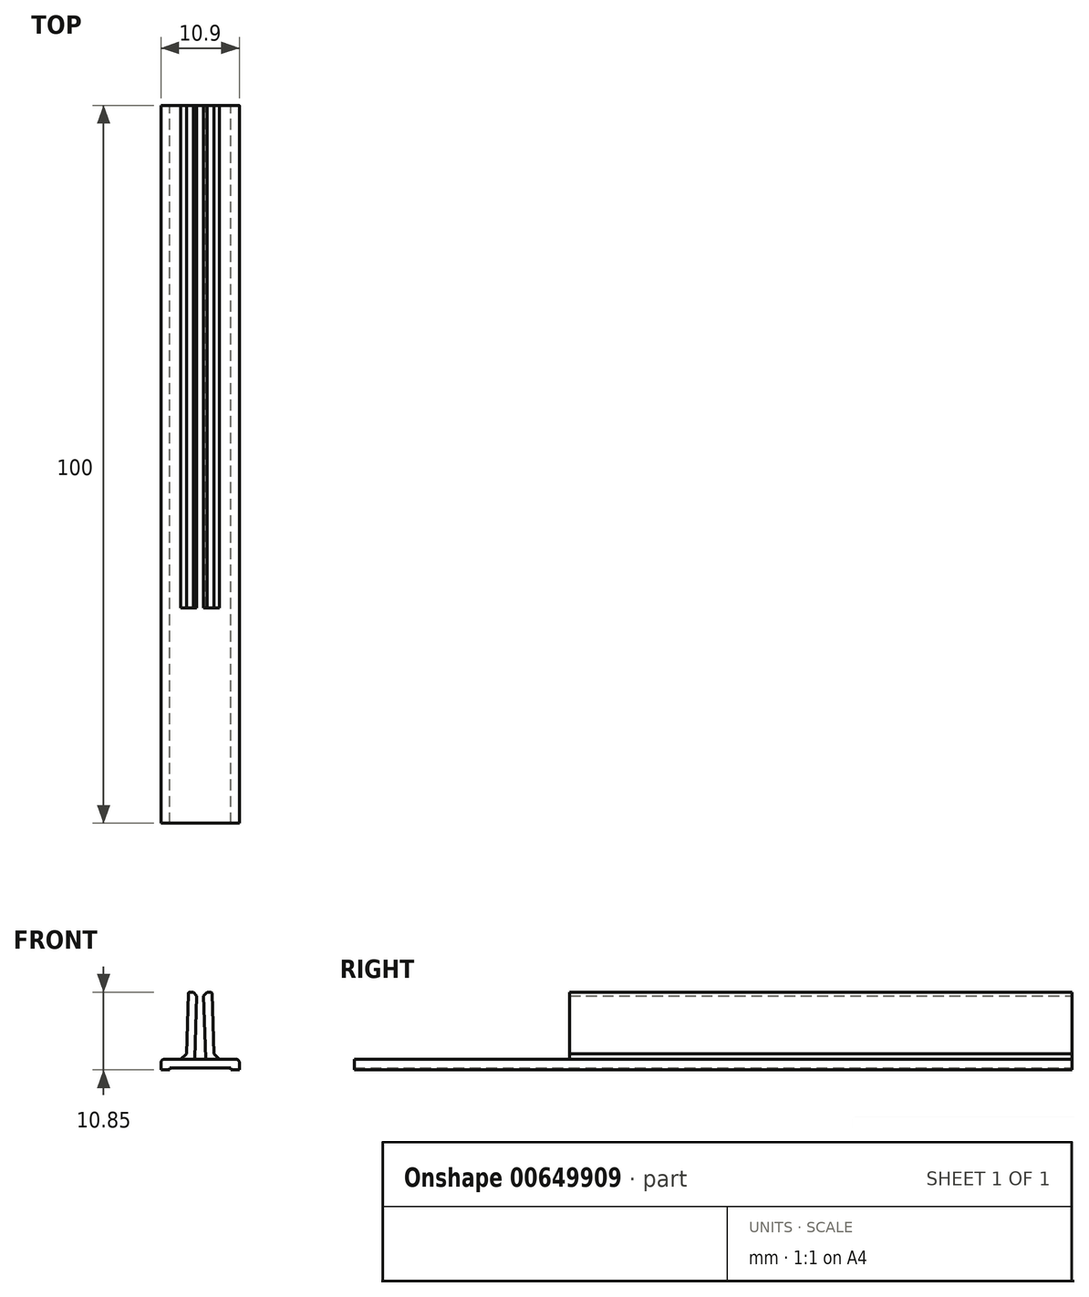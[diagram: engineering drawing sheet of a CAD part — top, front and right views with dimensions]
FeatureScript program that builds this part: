
annotation { "Feature Type Name" : "Feature", "Feature Type Description" : "" }
export const myFeature = defineFeature(function(context is Context, id is Id, definition is map)
    precondition{}
    {
        {
            var Q0;
            Q0=qCreatedBy(makeId("Front.planeOp"),FACE);
            var sketch = newSketch(context, id + "F0", { "sketchPlane" : qUnion([Q0])});
            skLineSegment(sketch, "E0.bottom", {"start": v(1.4, 5.75) * mm, "end": v(0.7, 5.75) * mm});
            skLineSegment(sketch, "E0.top", {"start": v(5.2, -5.1) * mm, "end": v(4.5, -5.1) * mm});
            skLineSegment(sketch, "E1", {"start": v(0, -3.6) * mm, "end": v(0.64, -3.6) * mm});
            skLineSegment(sketch, "E2", {"start": v(0.46, 5.5) * mm, "end": v(0.74, -3.5) * mm});
            skLineSegment(sketch, "E3", {"start": v(0.7, 5.75) * mm, "end": v(1.4, 5.75) * mm});
            skLineSegment(sketch, "E4", {"start": v(4.25, -4.8) * mm, "end": v(0, -4.8) * mm});
            skLineSegment(sketch, "E5", {"start": v(1.66, 5.5) * mm, "end": v(1.95, -3.6) * mm});
            skPoint(sketch, "E6.visualSharp", {"position": v(1.65, 5.75) * mm});
            skArc(sketch, "E6.filletArc", {"start": v(1.66, 5.5) * mm, "mid": v(1.58, 5.68) * mm, "end": v(1.4, 5.75) * mm});
            skPoint(sketch, "E7.visualSharp", {"position": v(1.95, -3.6) * mm});
            skPoint(sketch, "E8.visualSharp", {"position": v(0.75, -3.6) * mm});
            skArc(sketch, "E8.filletArc", {"start": v(0.64, -3.6) * mm, "mid": v(0.71, -3.56) * mm, "end": v(0.74, -3.5) * mm});
            skLineSegment(sketch, "E9", {"start": v(4.25, -4.8) * mm, "end": v(4.25, -5.1) * mm});
            skLineSegment(sketch, "E10", {"start": v(4.25, -5.1) * mm, "end": v(5.45, -5.1) * mm});
            skLineSegment(sketch, "E11", {"start": v(5.45, -5.1) * mm, "end": v(5.45, -4.85) * mm});
            skLineSegment(sketch, "E12", {"start": v(1.92, -2.85) * mm, "end": v(1.95, -3.6) * mm});
            skLineSegment(sketch, "E13", {"start": v(0.46, 5.5) * mm, "end": v(0.45, 5.74) * mm});
            skLineSegment(sketch, "E14", {"start": v(0.7, 5.75) * mm, "end": v(0.45, 5.74) * mm});
            skLineSegment(sketch, "E15", {"start": v(1.92, -2.85) * mm, "end": v(2.7, -3.6) * mm});
            skPoint(sketch, "E16.visualSharp", {"position": v(5.45, -3.6) * mm});
            skLineSegment(sketch, "E17", {"start": v(2.7, -3.6) * mm, "end": v(4.95, -3.6) * mm});
            skLineSegment(sketch, "E18", {"start": v(5.45, -5.1) * mm, "end": v(5.45, -4.1) * mm});
            skArc(sketch, "E19.filletArc", {"start": v(5.45, -4.1) * mm, "mid": v(5.3, -3.74) * mm, "end": v(4.95, -3.6) * mm});
            skLineSegment(sketch, "E20.MirrorCS", {"start": v(-0.46, 5.5) * mm, "end": v(-0.45, 5.74) * mm});
            skLineSegment(sketch, "E21.MirrorCS", {"start": v(-1.4, 5.75) * mm, "end": v(-0.7, 5.75) * mm});
            skLineSegment(sketch, "E22.MirrorCS", {"start": v(-0.7, 5.75) * mm, "end": v(-0.45, 5.74) * mm});
            skLineSegment(sketch, "E23.MirrorCS", {"start": v(-0.7, 5.75) * mm, "end": v(-1.4, 5.75) * mm});
            skArc(sketch, "E24.MirrorCS", {"start": v(-0.64, -3.6) * mm, "mid": v(-0.71, -3.56) * mm, "end": v(-0.74, -3.5) * mm});
            skLineSegment(sketch, "E25.MirrorCS", {"start": v(-1.92, -2.85) * mm, "end": v(-1.95, -3.6) * mm});
            skLineSegment(sketch, "E26.MirrorCS", {"start": v(-5.45, -5.1) * mm, "end": v(-5.45, -4.85) * mm});
            skArc(sketch, "E27.MirrorCS", {"start": v(-1.66, 5.5) * mm, "mid": v(-1.58, 5.68) * mm, "end": v(-1.4, 5.75) * mm});
            skLineSegment(sketch, "E28.MirrorCS", {"start": v(-5.2, -5.1) * mm, "end": v(-4.5, -5.1) * mm});
            skLineSegment(sketch, "E29.MirrorCS", {"start": v(-4.25, -4.8) * mm, "end": v(-4.25, -5.1) * mm});
            skLineSegment(sketch, "E30.MirrorCS", {"start": v(-1.92, -2.85) * mm, "end": v(-2.7, -3.6) * mm});
            skArc(sketch, "E31.MirrorCS", {"start": v(-5.45, -4.1) * mm, "mid": v(-5.3, -3.74) * mm, "end": v(-4.95, -3.6) * mm});
            skPoint(sketch, "E32.MirrorP", {"position": v(-5.45, -3.6) * mm});
            skLineSegment(sketch, "E33.MirrorCS", {"start": v(-4.25, -5.1) * mm, "end": v(-5.45, -5.1) * mm});
            skLineSegment(sketch, "E34.MirrorCS", {"start": v(-5.45, -5.1) * mm, "end": v(-5.45, -4.1) * mm});
            skLineSegment(sketch, "E35.MirrorCS", {"start": v(0, -3.6) * mm, "end": v(-0.64, -3.6) * mm});
            skPoint(sketch, "E36.MirrorP", {"position": v(-1.65, 5.75) * mm});
            skLineSegment(sketch, "E37.MirrorCS", {"start": v(-1.66, 5.5) * mm, "end": v(-1.95, -3.6) * mm});
            skPoint(sketch, "E38.MirrorP", {"position": v(-1.95, -3.6) * mm});
            skPoint(sketch, "E39.MirrorP", {"position": v(-0.75, -3.6) * mm});
            skLineSegment(sketch, "E40.MirrorCS", {"start": v(-4.25, -4.8) * mm, "end": v(0, -4.8) * mm});
            skLineSegment(sketch, "E41.MirrorCS", {"start": v(-2.7, -3.6) * mm, "end": v(-4.95, -3.6) * mm});
            skLineSegment(sketch, "E42.MirrorCS", {"start": v(-0.46, 5.5) * mm, "end": v(-0.74, -3.5) * mm});
            skSolve(sketch);
        }
        {
            var Q0;
            {var subQ4=sQuery(id+"F0.wireOp",EDGE,"E1");Q0=makeQuery(id+"F0.imprint","IMPRINT",FACE,{"disambiguationData":[TD([[makeQuery(id+"F0.imprint","IMPRINT",EDGE,{"derivedFrom":subQ4}),-1.0]])]});}
            extrude(context, id + "F1", {"entities" : qUnion([Q0]), "depth" : 100 * mm, "offsetDistance" : 25 * mm});
        }
        {
            var Q0;
            Q0=makeQuery(id+"F1.opExtrude","SWEPT_EDGE",EDGE,{"disambiguationData":[OSD([sQuery(id+"F0.wireOp",EDGE,"E20.MirrorCS"),sQuery(id+"F0.wireOp",EDGE,"E22.MirrorCS")])]});
            var Q1;
            Q1=makeQuery(id+"F1.opExtrude","SWEPT_EDGE",EDGE,{"disambiguationData":[OSD([sQuery(id+"F0.wireOp",EDGE,"E13"),sQuery(id+"F0.wireOp",EDGE,"E14")])]});
            chamfer(context, id + "F2", {"entities" : qUnion([Q0, Q1]), "width" : .5 * mm, "tangentPropagation" : true});
        }
        {
            var Q0;
            Q0=makeQuery(id+"F1.opExtrude","CAP_FACE",FACE,{"disambiguationData":[OSD([sQuery(id+"F0.wireOp",EDGE,"E1"),sQuery(id+"F0.wireOp",EDGE,"E2"),sQuery(id+"F0.wireOp",EDGE,"E3"),sQuery(id+"F0.wireOp",EDGE,"E4"),sQuery(id+"F0.wireOp",EDGE,"E5"),sQuery(id+"F0.wireOp",EDGE,"E6.filletArc"),sQuery(id+"F0.wireOp",EDGE,"E8.filletArc"),sQuery(id+"F0.wireOp",EDGE,"E9"),sQuery(id+"F0.wireOp",EDGE,"E10"),sQuery(id+"F0.wireOp",EDGE,"E13"),sQuery(id+"F0.wireOp",EDGE,"E14"),sQuery(id+"F0.wireOp",EDGE,"E15"),sQuery(id+"F0.wireOp",EDGE,"E17"),sQuery(id+"F0.wireOp",EDGE,"E18"),sQuery(id+"F0.wireOp",EDGE,"E19.filletArc"),sQuery(id+"F0.wireOp",EDGE,"E20.MirrorCS"),sQuery(id+"F0.wireOp",EDGE,"E22.MirrorCS"),sQuery(id+"F0.wireOp",EDGE,"E23.MirrorCS"),sQuery(id+"F0.wireOp",EDGE,"E24.MirrorCS"),sQuery(id+"F0.wireOp",EDGE,"E27.MirrorCS"),sQuery(id+"F0.wireOp",EDGE,"E29.MirrorCS"),sQuery(id+"F0.wireOp",EDGE,"E30.MirrorCS"),sQuery(id+"F0.wireOp",EDGE,"E31.MirrorCS"),sQuery(id+"F0.wireOp",EDGE,"E33.MirrorCS"),sQuery(id+"F0.wireOp",EDGE,"E34.MirrorCS"),sQuery(id+"F0.wireOp",EDGE,"E35.MirrorCS"),sQuery(id+"F0.wireOp",EDGE,"E37.MirrorCS"),sQuery(id+"F0.wireOp",EDGE,"E40.MirrorCS"),sQuery(id+"F0.wireOp",EDGE,"E41.MirrorCS"),sQuery(id+"F0.wireOp",EDGE,"E42.MirrorCS")])],"isStart":false});
            var sketch = newSketch(context, id + "F3", { "sketchPlane" : qUnion([Q0])});
            skLineSegment(sketch, "E43.1", {"start": v(2.7, -3.6) * mm, "end": v(4.95, -3.6) * mm});
            skLineSegment(sketch, "E44", {"start": v(0, -3.6) * mm, "end": v(4.95, -3.6) * mm});
            skLineSegment(sketch, "E45", {"start": v(4.95, -3.6) * mm, "end": v(4.95, 6.33) * mm});
            skLineSegment(sketch, "E46", {"start": v(4.95, 6.33) * mm, "end": v(0, 6.33) * mm});
            skLineSegment(sketch, "E47.MirrorCS", {"start": v(-2.7, -3.6) * mm, "end": v(-4.95, -3.6) * mm});
            skLineSegment(sketch, "E48.MirrorCS", {"start": v(-4.95, 6.33) * mm, "end": v(0, 6.33) * mm});
            skLineSegment(sketch, "E49.MirrorCS", {"start": v(0, -3.6) * mm, "end": v(-4.95, -3.6) * mm});
            skLineSegment(sketch, "E50.MirrorCS", {"start": v(-4.95, -3.6) * mm, "end": v(-4.95, 6.33) * mm});
            skSolve(sketch);
        }
        {
            var Q0;
            Q0 = qSketchRegion(id + "F3", true);
            extrude(context, id + "F4", {"entities" : qUnion([Q0]), "operationType" : NewBodyOperationType.REMOVE, "oppositeDirection" : true, "depth" : 30 * mm, "offsetDistance" : 25 * mm});
        }
    });
